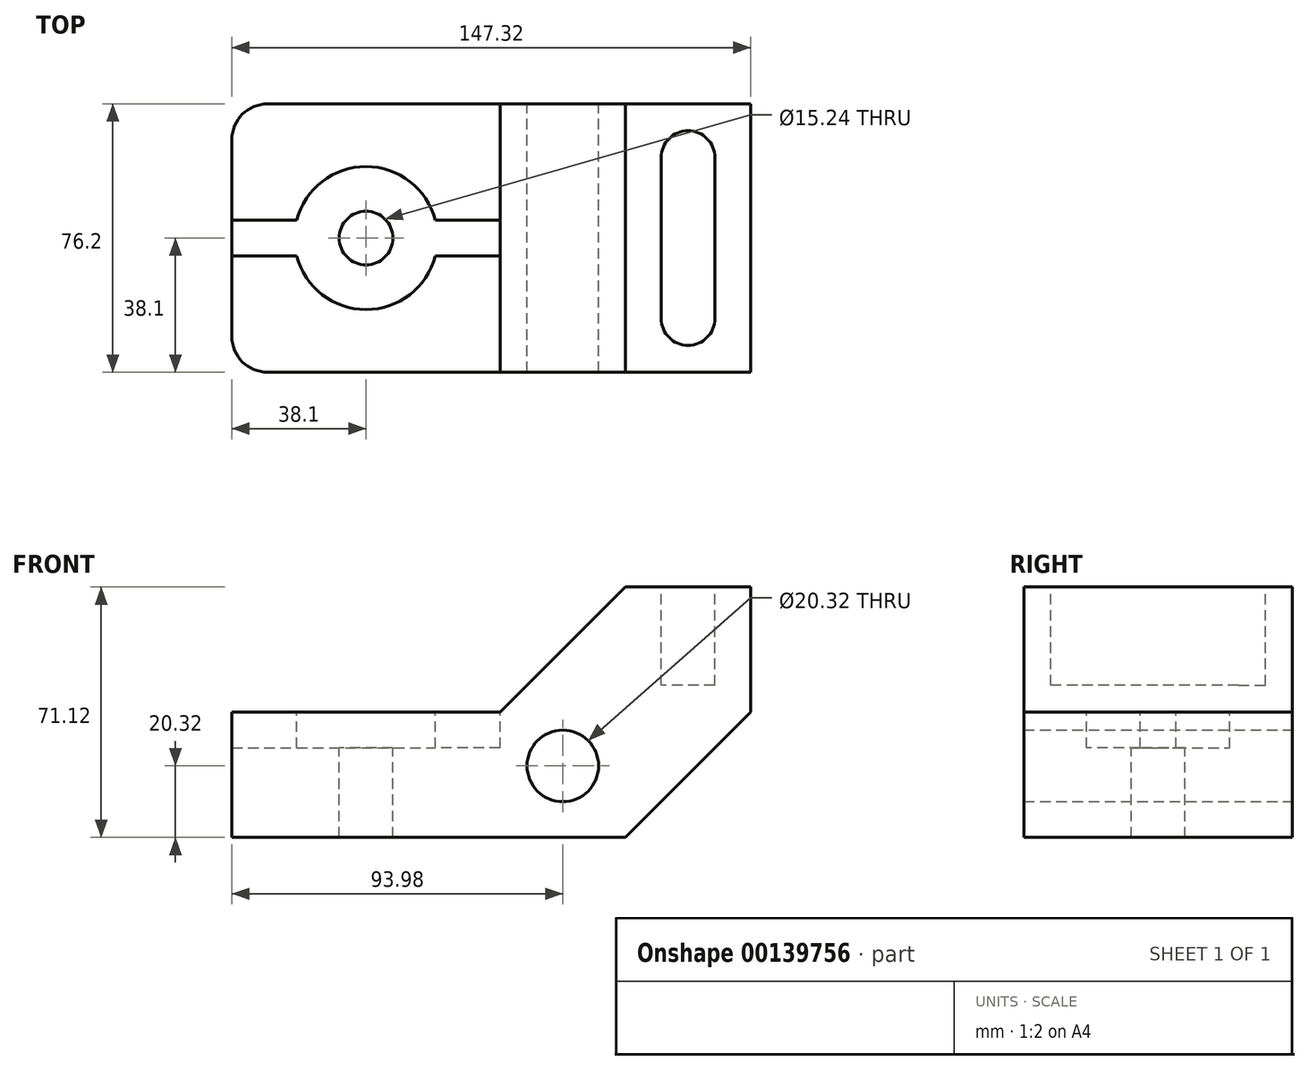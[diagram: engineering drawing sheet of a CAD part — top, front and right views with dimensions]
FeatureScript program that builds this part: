
annotation { "Feature Type Name" : "Feature", "Feature Type Description" : "" }
export const myFeature = defineFeature(function(context is Context, id is Id, definition is map)
    precondition{}
    {
        {
            var Q0;
            Q0=qCreatedBy(makeId("Front.planeOp"),FACE);
            var sketch = newSketch(context, id + "F0", { "sketchPlane" : qUnion([Q0])});
            skLineSegment(sketch, "E0", {"start": v(0, 0) * mm, "end": v(111.76, 0) * mm});
            skLineSegment(sketch, "E1", {"start": v(111.76, 0) * mm, "end": v(147.32, 35.56) * mm});
            skLineSegment(sketch, "E2", {"start": v(147.32, 35.56) * mm, "end": v(147.32, 71.12) * mm});
            skLineSegment(sketch, "E3", {"start": v(147.32, 71.12) * mm, "end": v(111.76, 71.12) * mm});
            skLineSegment(sketch, "E4", {"start": v(111.76, 71.12) * mm, "end": v(76.2, 35.56) * mm});
            skLineSegment(sketch, "E5", {"start": v(76.2, 35.56) * mm, "end": v(0, 35.56) * mm});
            skLineSegment(sketch, "E6", {"start": v(0, 35.56) * mm, "end": v(0, 0) * mm});
            skCircle(sketch, "E7", {"center": v(93.98, 20.32) * mm, "radius": 10.16 * mm});
            skSolve(sketch);
        }
        {
            var Q0;
            Q0=makeQuery(id+"F0.imprint","IMPRINT",FACE,{"disambiguationData":[TD([[makeQuery(id+"F0.imprint","IMPRINT",EDGE,{"derivedFrom":sQuery(id+"F0.wireOp",EDGE,"E0")}),1.0]])]});
            extrude(context, id + "F1", {"entities" : qUnion([Q0]), "depth" : 76.2 * mm});
        }
        {
            var Q0;
            Q0=makeQuery(id+"F1.opExtrude","SWEPT_FACE",FACE,{"disambiguationData":[OSD([sQuery(id+"F0.wireOp",EDGE,"E3")])]});
            var sketch = newSketch(context, id + "F2", { "sketchPlane" : qUnion([Q0])});
            skLineSegment(sketch, "E8", {"start": v(121.92, -15.24) * mm, "end": v(121.92, -60.96) * mm});
            skLineSegment(sketch, "E9", {"start": v(137.16, -15.24) * mm, "end": v(137.16, -60.96) * mm});
            skArc(sketch, "E10", {"start": v(137.16, -15.24) * mm, "mid": v(129.54, -7.62) * mm, "end": v(121.92, -15.24) * mm});
            skArc(sketch, "E11", {"start": v(121.92, -60.96) * mm, "mid": v(129.54, -68.58) * mm, "end": v(137.16, -60.96) * mm});
            skSolve(sketch);
        }
        {
            var Q0;
            Q0=makeQuery(id+"F2.imprint","IMPRINT",FACE,{"disambiguationData":[TD([[makeQuery(id+"F2.imprint","IMPRINT",EDGE,{"derivedFrom":sQuery(id+"F2.wireOp",EDGE,"E8")}),1.0]])]});
            extrude(context, id + "F3", {"entities" : qUnion([Q0]), "operationType" : NewBodyOperationType.REMOVE, "oppositeDirection" : true, "depth" : 27.94 * mm});
        }
        {
            var Q0;
            Q0=makeQuery(id+"F1.opExtrude","SWEPT_FACE",FACE,{"disambiguationData":[OSD([sQuery(id+"F0.wireOp",EDGE,"E5")])]});
            var sketch = newSketch(context, id + "F4", { "sketchPlane" : qUnion([Q0])});
            skLineSegment(sketch, "E12.bottom", {"start": v(0, 0) * mm, "end": v(76.2, 0) * mm});
            skLineSegment(sketch, "E12.top", {"start": v(0, -76.2) * mm, "end": v(76.2, -76.2) * mm});
            skLineSegment(sketch, "E12.left", {"start": v(0, 0) * mm, "end": v(0, -76.2) * mm});
            skLineSegment(sketch, "E12.right", {"start": v(76.2, 0) * mm, "end": v(76.2, -76.2) * mm});
            skLineSegment(sketch, "E13", {"start": v(18.43, -43.18) * mm, "end": v(0, -43.18) * mm});
            skLineSegment(sketch, "E14", {"start": v(0, -43.18) * mm, "end": v(0, -33.02) * mm});
            skLineSegment(sketch, "E15", {"start": v(0, -33.02) * mm, "end": v(18.43, -33.02) * mm});
            skLineSegment(sketch, "E16", {"start": v(76.2, -33.02) * mm, "end": v(57.77, -33.02) * mm});
            skLineSegment(sketch, "E17", {"start": v(76.2, -33.02) * mm, "end": v(76.2, -43.18) * mm});
            skLineSegment(sketch, "E18", {"start": v(76.2, -43.18) * mm, "end": v(57.77, -43.18) * mm});
            skArc(sketch, "E19", {"start": v(57.77, -33.02) * mm, "mid": v(38.1, -17.78) * mm, "end": v(18.43, -33.02) * mm});
            skArc(sketch, "E20", {"start": v(18.43, -43.18) * mm, "mid": v(38.1, -58.42) * mm, "end": v(57.77, -43.18) * mm});
            skCircle(sketch, "E21", {"center": v(38.1, -38.1) * mm, "radius": 7.62 * mm});
            skSolve(sketch);
        }
        {
            var Q0;
            Q0=makeQuery(id+"F4.imprint","IMPRINT",FACE,{"disambiguationData":[TD([[makeQuery(id+"F4.imprint","IMPRINT",EDGE,{"derivedFrom":sQuery(id+"F4.wireOp",EDGE,"E13")}),-1.0]])]});
            extrude(context, id + "F5", {"entities" : qUnion([Q0]), "operationType" : NewBodyOperationType.REMOVE, "oppositeDirection" : true, "depth" : 10.16 * mm});
        }
        {
            var Q0;
            Q0=makeQuery(id+"F4.imprint","IMPRINT",FACE,{"disambiguationData":[TD([[makeQuery(id+"F4.imprint","IMPRINT",EDGE,{"derivedFrom":sQuery(id+"F4.wireOp",EDGE,"E21")}),1.0]])]});
            var Q1;
            Q1=sQuery(id+"F4.wireOp",EDGE,"E21");
            extrude(context, id + "F6", {"entities" : qUnion([Q0]), "operationType" : NewBodyOperationType.REMOVE, "surfaceEntities" : qUnion([Q1]), "endBound" : BoundingType.THROUGH_ALL, "oppositeDirection" : true, "depth" : 25.4 * mm});
        }
        {
            var Q0;
            Q0=makeQuery(id+"F1.opExtrude","CAP_EDGE",EDGE,{"disambiguationData":[OSD([sQuery(id+"F0.wireOp",EDGE,"E6")])],"isStart":false});
            var Q1;
            Q1=makeQuery(id+"F1.opExtrude","CAP_EDGE",EDGE,{"disambiguationData":[OSD([sQuery(id+"F0.wireOp",EDGE,"E6")])],"isStart":true});
            fillet(context, id + "F7", {"entities" : qUnion([Q0, Q1]), "radius" : 10.16 * mm, "tangentPropagation" : true, "allowEdgeOverflow" : false});
        }
    });
